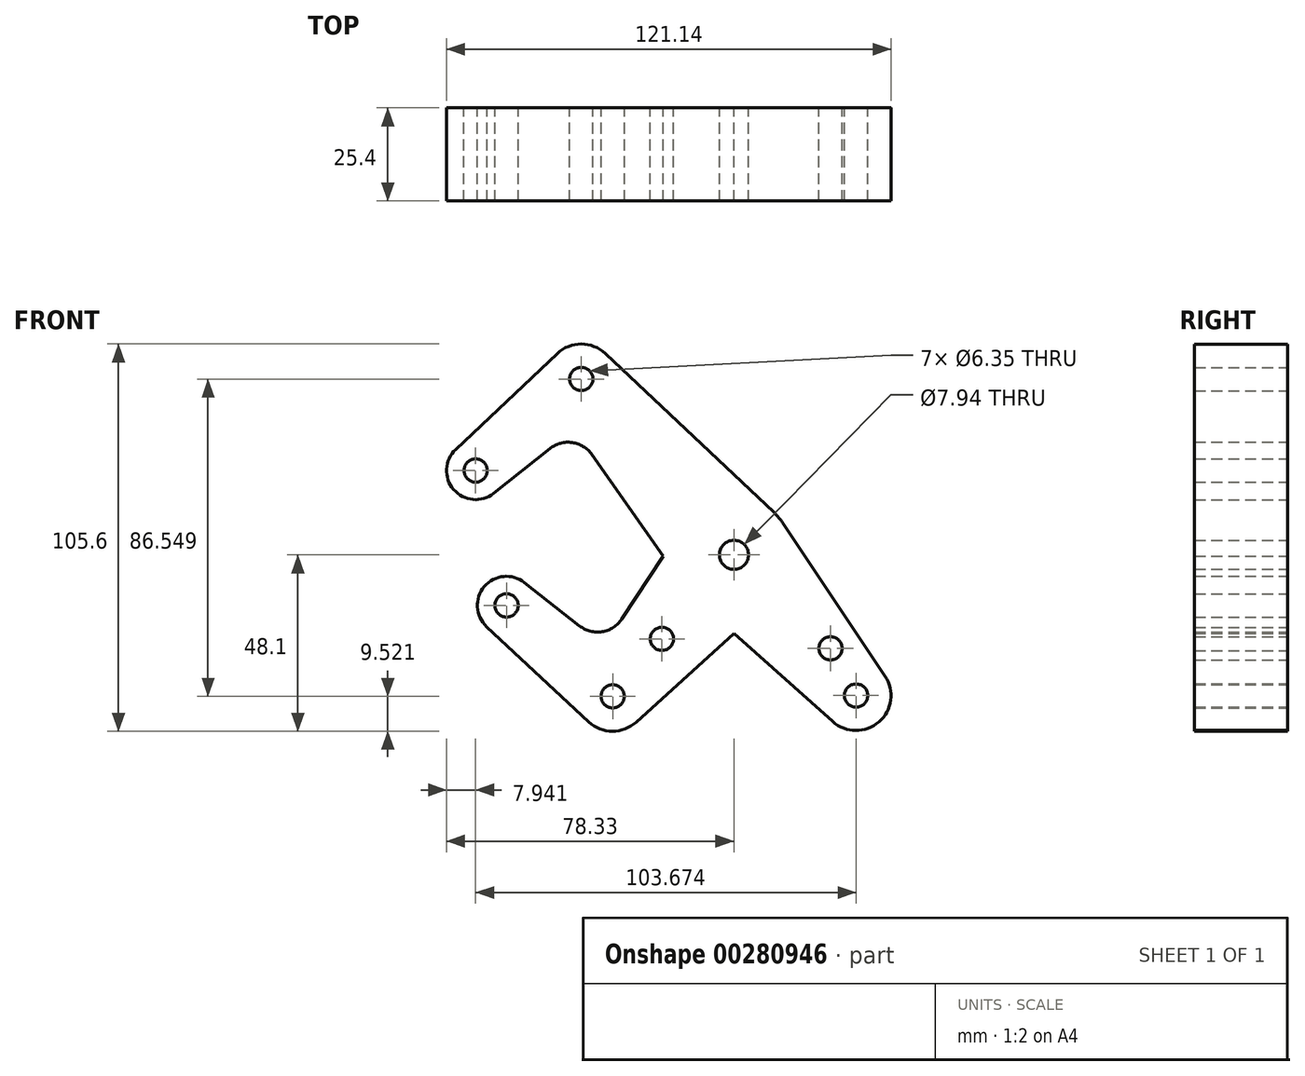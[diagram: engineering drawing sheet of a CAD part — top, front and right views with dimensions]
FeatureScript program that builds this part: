
annotation { "Feature Type Name" : "Feature", "Feature Type Description" : "" }
export const myFeature = defineFeature(function(context is Context, id is Id, definition is map)
    precondition{}
    {
        {
            var Q0;
            Q0=qCreatedBy(makeId("Front.planeOp"),FACE);
            var sketch = newSketch(context, id + "F0", { "sketchPlane" : qUnion([Q0])});
            skLineSegment(sketch, "E0", {"start": v(-41.6, 47.97) * mm, "end": v(41.6, -47.97) * mm, "construction": true});
            skCircle(sketch, "E1", {"center": v(0, 0) * mm, "radius": 3.18 * mm});
            skCircle(sketch, "E2", {"center": v(33.29, -38.38) * mm, "radius": 3.18 * mm});
            skCircle(sketch, "E3", {"center": v(-41.6, 47.97) * mm, "radius": 3.18 * mm});
            skCircle(sketch, "E4", {"center": v(-70.39, 23) * mm, "radius": 3.18 * mm});
            skLineSegment(sketch, "E5", {"start": v(-41.6, 47.97) * mm, "end": v(-70.39, 23) * mm, "construction": true});
            skCircle(sketch, "E6", {"center": v(33.29, -38.38) * mm, "radius": 9.53 * mm});
            skCircle(sketch, "E7", {"center": v(-70.39, 23) * mm, "radius": 7.94 * mm});
            skCircle(sketch, "E8", {"center": v(-41.6, 47.97) * mm, "radius": 9.53 * mm});
            skLineSegment(sketch, "E9", {"start": v(-75.83, 28.78) * mm, "end": v(-48.14, 54.9) * mm});
            skLineSegment(sketch, "E10", {"start": v(-65.44, 16.8) * mm, "end": v(-50.15, 28.98) * mm});
            skCircle(sketch, "E11", {"center": v(0, 0) * mm, "radius": 15.88 * mm});
            skLineSegment(sketch, "E12", {"start": v(-35.07, 54.9) * mm, "end": v(10.9, 11.55) * mm});
            skLineSegment(sketch, "E13", {"start": v(-38.72, 27.35) * mm, "end": v(-12.97, -9.15) * mm});
            skLineSegment(sketch, "E14", {"start": v(-10.6, -11.82) * mm, "end": v(26.93, -45.47) * mm});
            skLineSegment(sketch, "E15", {"start": v(13.2, 8.82) * mm, "end": v(41.2, -33.08) * mm});
            skArc(sketch, "E16.filletArc", {"start": v(-38.72, 27.35) * mm, "mid": v(-44.08, 30.63) * mm, "end": v(-50.15, 28.98) * mm});
            skLineSegment(sketch, "E17", {"start": v(0, 0) * mm, "end": v(-33.05, -38.58) * mm, "construction": true});
            skLineSegment(sketch, "E18", {"start": v(-33.05, -38.58) * mm, "end": v(-61.98, -13.8) * mm, "construction": true});
            skCircle(sketch, "E19", {"center": v(-61.98, -13.8) * mm, "radius": 3.18 * mm});
            skCircle(sketch, "E20", {"center": v(-33.05, -38.58) * mm, "radius": 3.18 * mm});
            skCircle(sketch, "E21", {"center": v(-61.98, -13.8) * mm, "radius": 7.94 * mm});
            skCircle(sketch, "E22", {"center": v(-33.05, -38.58) * mm, "radius": 9.53 * mm});
            skLineSegment(sketch, "E23", {"start": v(-57.08, -7.55) * mm, "end": v(-42.08, -19.35) * mm});
            skLineSegment(sketch, "E24", {"start": v(-67.4, -19.6) * mm, "end": v(-39.54, -45.55) * mm});
            skLineSegment(sketch, "E25", {"start": v(-13.25, 8.74) * mm, "end": v(-30.55, -17.48) * mm});
            skLineSegment(sketch, "E26", {"start": v(10.67, -11.75) * mm, "end": v(-26.65, -45.63) * mm});
            skArc(sketch, "E27.filletArc", {"start": v(-42.08, -19.35) * mm, "mid": v(-35.9, -20.95) * mm, "end": v(-30.55, -17.48) * mm});
            skCircle(sketch, "E28", {"center": v(-19.62, -22.9) * mm, "radius": 3.18 * mm});
            skCircle(sketch, "E29", {"center": v(26.32, -25.5) * mm, "radius": 3.18 * mm});
            skLineSegment(sketch, "E30", {"start": v(26.32, -25.5) * mm, "end": v(23.92, -27.58) * mm, "construction": true});
            skCircle(sketch, "E31", {"center": v(0, 0) * mm, "radius": 3.97 * mm});
            skSolve(sketch);
        }
        {
            var Q0;
            Q0 = qSketchRegion(id + "F0", true);
            extrude(context, id + "F1", {"entities" : qUnion([Q0]), "depth" : 25.4 * mm});
        }
    });
